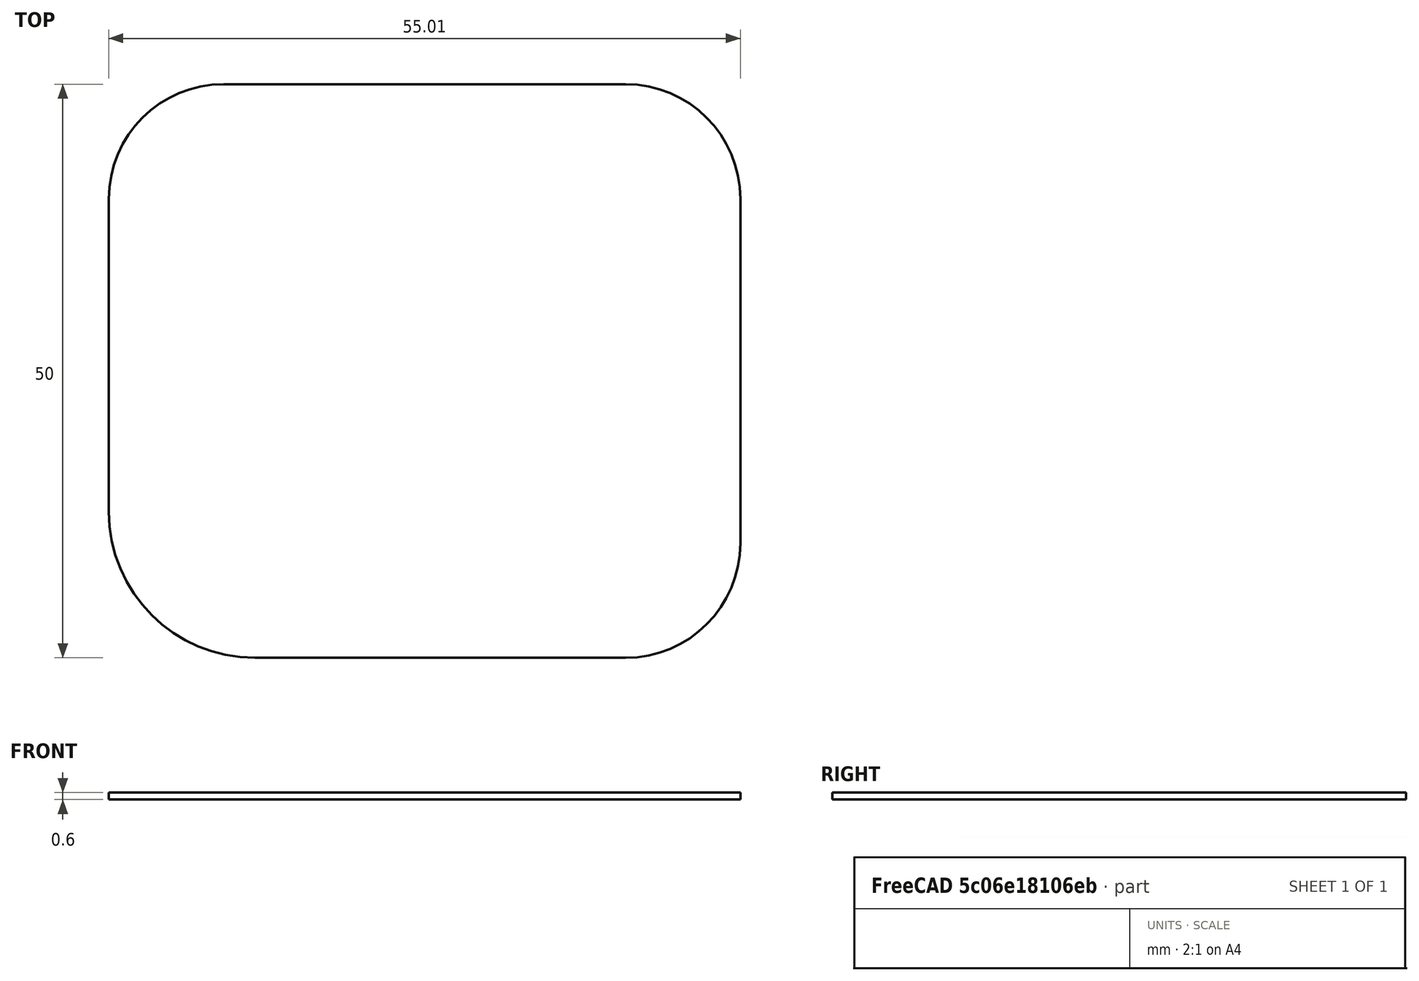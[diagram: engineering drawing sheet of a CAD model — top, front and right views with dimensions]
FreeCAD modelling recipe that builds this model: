
FCSTD DOCUMENT  (FreeCAD 0.21R33694 (Git))
Label: 生活阳台瓷砖修补片-5×.5.5mm
License: All rights reserved
LicenseURL: http://en.wikipedia.org/wiki/All_rights_reserved
objects: Sketcher::SketchObject×1, PartDesign::Pad×1, PartDesign::Body×1
note: 4 computed .brp shape members not serialized (recipe doc carries the construction recipe); baked Part::Feature solids carry a one-line shape summary decoded from their .brp

FEATURE [Sketcher::SketchObject] Sketch
  FullyConstrained = true
  MapMode = 5
  Support = -> [XY_Plane]
  sketch-geometry (8):
    g0: LineSegment StartX=-18.865 StartY=25 StartZ=0 EndX=16.135 EndY=25 EndZ=0
    g1: LineSegment StartX=26.135 StartY=15 StartZ=0 EndX=26.135 EndY=-15 EndZ=0
    g2: LineSegment StartX=16.135 StartY=-25 StartZ=0 EndX=-16.135 EndY=-25 EndZ=0
    g3: LineSegment StartX=-28.865 StartY=-12.27 StartZ=0 EndX=-28.865 EndY=15 EndZ=0
    g4: ArcOfCircle CenterX=-18.865 CenterY=15 CenterZ=0 NormalX=0 NormalY=0 NormalZ=1 AngleXU=0 Radius=10 StartAngle=1.5708 EndAngle=3.14159
    g5: ArcOfCircle CenterX=16.135 CenterY=15 CenterZ=0 NormalX=0 NormalY=0 NormalZ=1 AngleXU=0 Radius=10 StartAngle=0 EndAngle=1.5708
    g6: ArcOfCircle CenterX=16.135 CenterY=-15 CenterZ=0 NormalX=0 NormalY=0 NormalZ=1 AngleXU=0 Radius=10 StartAngle=4.71239 EndAngle=6.28319
    g7: ArcOfCircle CenterX=-16.135 CenterY=-12.27 CenterZ=0 NormalX=0 NormalY=0 NormalZ=1 AngleXU=0 Radius=12.73 StartAngle=3.14159 EndAngle=4.71239
  constraints (19):
    c: Horizontal(g0)
    c: Horizontal(g2)
    c: Vertical(g1)
    c: Vertical(g3)
    c: Tangent(g3,g4) = 1.5708
    c: Tangent(g0,g4) = 1.5708
    c: Tangent(g1,g5) = 1.5708
    c: Tangent(g0,g5) = 1.5708
    c: Tangent(g2,g6) = 1.5708
    c: Tangent(g1,g6) = 1.5708
    c: Tangent(g3,g7) = 1.5708
    c: Tangent(g2,g7) = 1.5708
    c: Distance(g3,g1) = 55
    c: Distance(g2,g0) = 50
    c: Radius(g4) = 10
    c: Radius(g7) = 12.73
    c: Radius(g6) = 10
    c: Radius(g5) = 10
    c: Symmetric(g2,g0,g-1)
FEATURE [PartDesign::Pad] Pad
  Direction = (0,0,1)
  Length = 0.6
  Length2 = 10
  Profile = -> Sketch
  ReferenceAxis = -> Sketch [N_Axis]
  Type = 0
FEATURE [PartDesign::Body] Body  label="实体"
  Group = -> [Sketch,Pad]
  Origin = -> Origin
  Tip = -> Pad
